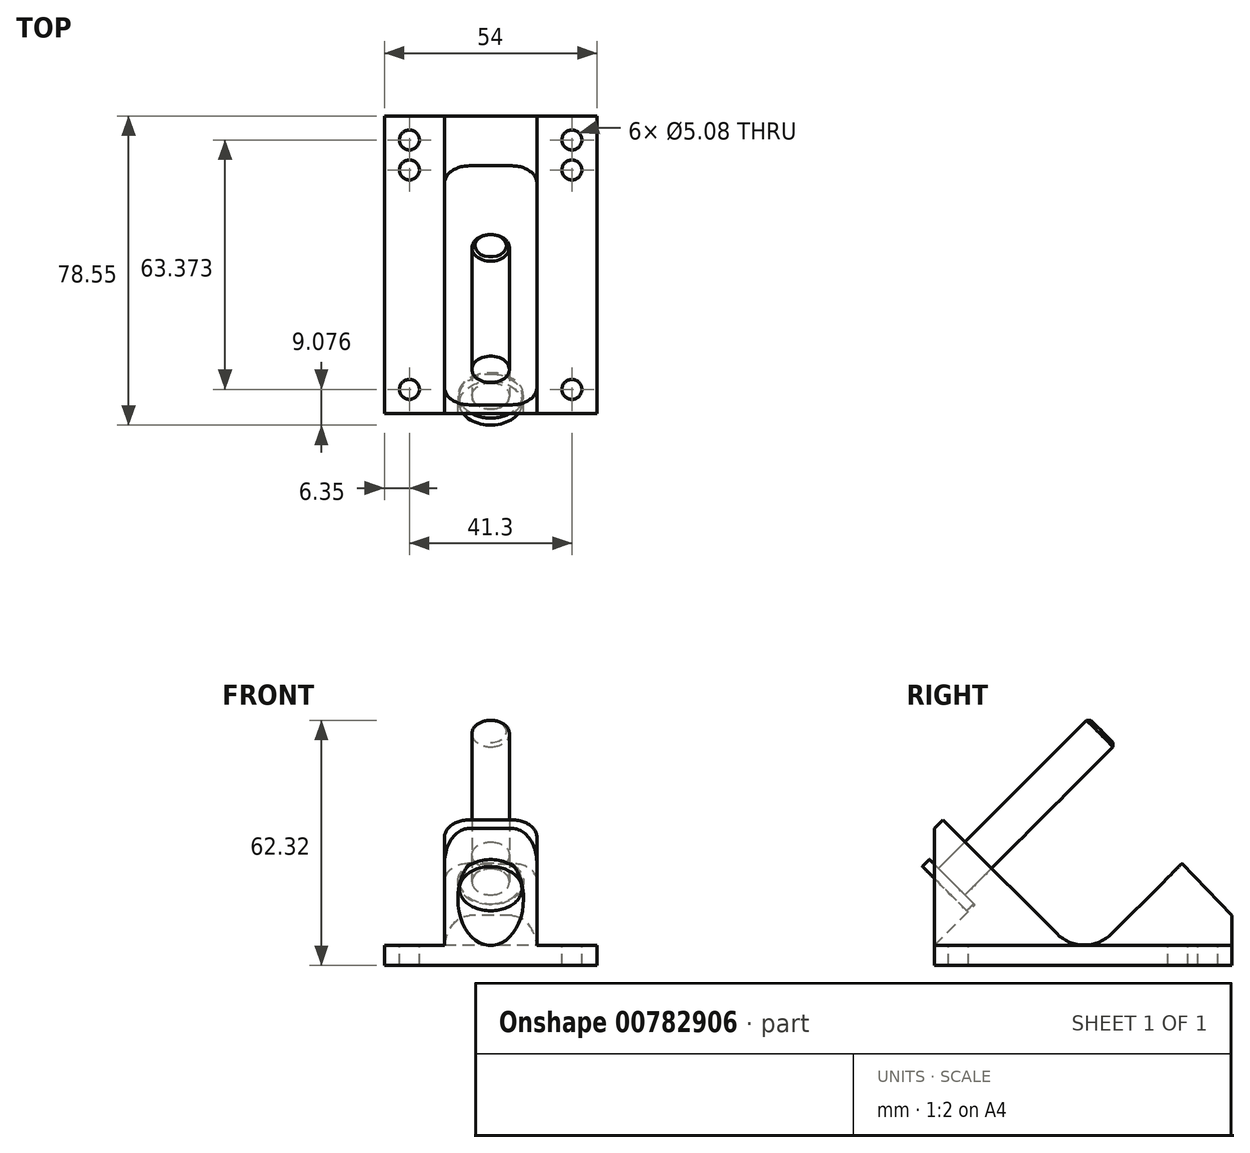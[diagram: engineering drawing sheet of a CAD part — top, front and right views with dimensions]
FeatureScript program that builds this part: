
annotation { "Feature Type Name" : "Feature", "Feature Type Description" : "" }
export const myFeature = defineFeature(function(context is Context, id is Id, definition is map)
    precondition{}
    {
        {
            var Q0;
            Q0=qCreatedBy(makeId("Right.planeOp"),FACE);
            var sketch = newSketch(context, id + "F0", { "sketchPlane" : qUnion([Q0])});
            skLineSegment(sketch, "E0", {"start": v(0, 0) * mm, "end": v(0, 34.86) * mm});
            skLineSegment(sketch, "E1", {"start": v(0, 34.86) * mm, "end": v(2.18, 37.04) * mm});
            skLineSegment(sketch, "E2", {"start": v(2.18, 37.04) * mm, "end": v(38.1, 1.12) * mm});
            skLineSegment(sketch, "E3", {"start": v(38.1, 1.12) * mm, "end": v(62.9, 25.92) * mm});
            skLineSegment(sketch, "E4", {"start": v(62.9, 25.92) * mm, "end": v(75.57, 12.7) * mm});
            skLineSegment(sketch, "E5", {"start": v(75.57, 12.7) * mm, "end": v(75.57, 0) * mm});
            skLineSegment(sketch, "E6", {"start": v(75.57, 0) * mm, "end": v(0, 0) * mm});
            skLineSegment(sketch, "E7", {"start": v(11.16, 28.06) * mm, "end": v(24.63, 41.53) * mm, "construction": true});
            skLineSegment(sketch, "E8", {"start": v(24.63, 41.53) * mm, "end": v(51.57, 14.59) * mm, "construction": true});
            skLineSegment(sketch, "E9", {"start": v(51.57, 14.59) * mm, "end": v(60.55, 5.6) * mm, "construction": true});
            skLineSegment(sketch, "E10", {"start": v(60.55, 5.6) * mm, "end": v(65.94, 11) * mm, "construction": true});
            skLineSegment(sketch, "E11", {"start": v(65.94, 11) * mm, "end": v(56.96, 19.98) * mm, "construction": true});
            skLineSegment(sketch, "E12", {"start": v(24.63, 41.53) * mm, "end": v(11.16, 55) * mm, "construction": true});
            skCircle(sketch, "E13", {"center": v(11.16, 55) * mm, "radius": 4 * mm, "construction": true});
            skLineSegment(sketch, "E14", {"start": v(60.55, 5.6) * mm, "end": v(55.16, 0.22) * mm, "construction": true});
            skLineSegment(sketch, "E15", {"start": v(55.16, 0.22) * mm, "end": v(46.18, 9.2) * mm, "construction": true});
            skCircle(sketch, "E16", {"center": v(54.26, 11.9) * mm, "radius": 5.08 * mm, "construction": true});
            skSolve(sketch);
        }
        {
            var Q0;
            Q0 = qSketchRegion(id + "F0", true);
            extrude(context, id + "F1", {"entities" : qUnion([Q0]), "depth" : 27 * mm, "offsetDistance" : 25.4 * mm});
        }
        {
            var Q0;
            Q0=makeQuery(id+"F1.opExtrude","SWEPT_EDGE",EDGE,{"disambiguationData":[OSD([sQuery(id+"F0.wireOp",EDGE,"E2"),sQuery(id+"F0.wireOp",EDGE,"E3")])]});
            fillet(context, id + "F2", {"entities" : qUnion([Q0]), "radius" : 9.9 * mm, "tangentPropagation" : true, "allowEdgeOverflow" : false});
        }
        {
            var Q0;
            Q0=makeQuery(id+"F1.opExtrude","CAP_FACE",FACE,{"disambiguationData":[OSD([sQuery(id+"F0.wireOp",EDGE,"E0"),sQuery(id+"F0.wireOp",EDGE,"E1"),sQuery(id+"F0.wireOp",EDGE,"E2"),sQuery(id+"F0.wireOp",EDGE,"E3"),sQuery(id+"F0.wireOp",EDGE,"E4"),sQuery(id+"F0.wireOp",EDGE,"E5"),sQuery(id+"F0.wireOp",EDGE,"E6")])],"isStart":false});
            var sketch = newSketch(context, id + "F3", { "sketchPlane" : qUnion([Q0])});
            skLineSegment(sketch, "E17.bottom", {"start": v(0, 5.08) * mm, "end": v(75.71, 5.08) * mm});
            skLineSegment(sketch, "E17.top", {"start": v(0, 37.04) * mm, "end": v(75.71, 37.04) * mm});
            skLineSegment(sketch, "E17.left", {"start": v(0, 5.08) * mm, "end": v(0, 37.04) * mm});
            skLineSegment(sketch, "E17.right", {"start": v(75.71, 5.08) * mm, "end": v(75.71, 37.04) * mm});
            skSolve(sketch);
        }
        {
            var Q0;
            Q0 = qSketchRegion(id + "F3", true);
            extrude(context, id + "F4", {"entities" : qUnion([Q0]), "operationType" : NewBodyOperationType.REMOVE, "oppositeDirection" : true, "depth" : 15.24 * mm, "offsetDistance" : 25.4 * mm});
        }
        {
            var Q0;
            Q0=makeQuery(id+"F4.boolean.opBoolean","COPY",FACE,{"derivedFrom":makeQuery(id+"F4.opExtrude","SWEPT_FACE",FACE,{"disambiguationData":[OSD([sQuery(id+"F3.wireOp",EDGE,"E17.bottom")])]})});
            var sketch = newSketch(context, id + "F5", { "sketchPlane" : qUnion([Q0])});
            skLineSegment(sketch, "E18", {"start": v(20.65, 69.47) * mm, "end": v(20.65, 61.85) * mm, "construction": true});
            skLineSegment(sketch, "E19", {"start": v(20.65, 61.85) * mm, "end": v(20.65, 6.1) * mm, "construction": true});
            skCircle(sketch, "E20", {"center": v(20.65, 69.47) * mm, "radius": 2.54 * mm});
            skCircle(sketch, "E21", {"center": v(20.65, 61.85) * mm, "radius": 2.54 * mm});
            skCircle(sketch, "E22", {"center": v(20.65, 6.1) * mm, "radius": 2.54 * mm});
            skSolve(sketch);
        }
        {
            var Q0;
            Q0 = qSketchRegion(id + "F5", true);
            extrude(context, id + "F6", {"entities" : qUnion([Q0]), "operationType" : NewBodyOperationType.REMOVE, "endBound" : BoundingType.THROUGH_ALL, "oppositeDirection" : true, "depth" : 25.4 * mm, "offsetDistance" : 25.4 * mm});
        }
        {
            var Q0;
            Q0=makeQuery(id+"F1.opExtrude","SWEPT_BODY",BODY,{"disambiguationData":[OSD([sQuery(id+"F0.wireOp",EDGE,"E0"),sQuery(id+"F0.wireOp",EDGE,"E1"),sQuery(id+"F0.wireOp",EDGE,"E2"),sQuery(id+"F0.wireOp",EDGE,"E3"),sQuery(id+"F0.wireOp",EDGE,"E4"),sQuery(id+"F0.wireOp",EDGE,"E5"),sQuery(id+"F0.wireOp",EDGE,"E6")])]});
            var Q1;
            Q1=makeQuery(id+"F0.imprint","IMPRINT",FACE,{"disambiguationData":[TD([[makeQuery(id+"F0.imprint","IMPRINT",EDGE,{"derivedFrom":sQuery(id+"F0.wireOp",EDGE,"E0")}),-1.0]])]});
            mirror(context, id + "F7", {"operationType" : NewBodyOperationType.ADD, "entities" : qUnion([Q0]), "mirrorPlane" : qUnion([Q1])});
        }
        {
            var Q0;
            Q0=makeQuery(id+"F7.opPattern","COPY",EDGE,{"derivedFrom":makeQuery(id+"F4.boolean.opBoolean","INTERSECT",EDGE,{"derivedFrom":[makeQuery(id+"F1.opExtrude","SWEPT_FACE",FACE,{"disambiguationData":[OSD([sQuery(id+"F0.wireOp",EDGE,"E4")])]}),makeQuery(id+"F4.opExtrude","CAP_FACE",FACE,{"disambiguationData":[OSD([sQuery(id+"F3.wireOp",EDGE,"E17.bottom"),sQuery(id+"F3.wireOp",EDGE,"E17.top"),sQuery(id+"F3.wireOp",EDGE,"E17.left"),sQuery(id+"F3.wireOp",EDGE,"E17.right")])],"isStart":false})]}),"instanceName":"1"});
            var Q1;
            Q1=makeQuery(id+"F4.boolean.opBoolean","INTERSECT",EDGE,{"derivedFrom":[makeQuery(id+"F1.opExtrude","SWEPT_FACE",FACE,{"disambiguationData":[OSD([sQuery(id+"F0.wireOp",EDGE,"E4")])]}),makeQuery(id+"F4.opExtrude","CAP_FACE",FACE,{"disambiguationData":[OSD([sQuery(id+"F3.wireOp",EDGE,"E17.bottom"),sQuery(id+"F3.wireOp",EDGE,"E17.top"),sQuery(id+"F3.wireOp",EDGE,"E17.left"),sQuery(id+"F3.wireOp",EDGE,"E17.right")])],"isStart":false})]});
            var Q2;
            Q2=makeQuery(id+"F7.opPattern","COPY",EDGE,{"derivedFrom":makeQuery(id+"F4.boolean.opBoolean","INTERSECT",EDGE,{"derivedFrom":[makeQuery(id+"F1.opExtrude","SWEPT_FACE",FACE,{"disambiguationData":[OSD([sQuery(id+"F0.wireOp",EDGE,"E1")])]}),makeQuery(id+"F4.opExtrude","CAP_FACE",FACE,{"disambiguationData":[OSD([sQuery(id+"F3.wireOp",EDGE,"E17.bottom"),sQuery(id+"F3.wireOp",EDGE,"E17.top"),sQuery(id+"F3.wireOp",EDGE,"E17.left"),sQuery(id+"F3.wireOp",EDGE,"E17.right")])],"isStart":false})]}),"instanceName":"1"});
            var Q3;
            Q3=makeQuery(id+"F4.boolean.opBoolean","INTERSECT",EDGE,{"derivedFrom":[makeQuery(id+"F1.opExtrude","SWEPT_FACE",FACE,{"disambiguationData":[OSD([sQuery(id+"F0.wireOp",EDGE,"E1")])]}),makeQuery(id+"F4.opExtrude","CAP_FACE",FACE,{"disambiguationData":[OSD([sQuery(id+"F3.wireOp",EDGE,"E17.bottom"),sQuery(id+"F3.wireOp",EDGE,"E17.top"),sQuery(id+"F3.wireOp",EDGE,"E17.left"),sQuery(id+"F3.wireOp",EDGE,"E17.right")])],"isStart":false})]});
            fillet(context, id + "F8", {"entities" : qUnion([Q0, Q1, Q2, Q3]), "radius" : 6.35 * mm, "tangentPropagation" : true, "allowEdgeOverflow" : false});
        }
        {
            var Q0;
            Q0=qCreatedBy(makeId("Right.planeOp"),FACE);
            var sketch = newSketch(context, id + "F9", { "sketchPlane" : qUnion([Q0])});
            skLineSegment(sketch, "E23.0", {"start": v(11.16, 28.06) * mm, "end": v(24.63, 41.53) * mm, "construction": true});
            skLineSegment(sketch, "E24", {"start": v(11.16, 28.06) * mm, "end": v(7.8, 31.43) * mm});
            skLineSegment(sketch, "E25", {"start": v(7.8, 31.43) * mm, "end": v(1.06, 24.7) * mm});
            skLineSegment(sketch, "E26", {"start": v(1.06, 24.7) * mm, "end": v(-1.48, 27.22) * mm});
            skLineSegment(sketch, "E27", {"start": v(-1.48, 27.22) * mm, "end": v(-14.35, 14.35) * mm});
            skLineSegment(sketch, "E28", {"start": v(-14.35, 14.35) * mm, "end": v(-8.45, 8.45) * mm});
            skLineSegment(sketch, "E29", {"start": v(-8.45, 8.45) * mm, "end": v(11.16, 28.06) * mm});
            skLineSegment(sketch, "E30", {"start": v(-8.45, 8.45) * mm, "end": v(0, 0) * mm, "construction": true});
            skLineSegment(sketch, "E31.0", {"start": v(2.18, 37.04) * mm, "end": v(38.1, 1.12) * mm});
            skSolve(sketch);
        }
        {
            var Q0;
            Q0 = qSketchRegion(id + "F9", true);
            var Q1;
            Q1=sQuery(id+"F9.wireOp",EDGE,"E23.0");
            revolve(context, id + "F10", {"operationType" : NewBodyOperationType.REMOVE, "surfaceOperationType" : NewSurfaceOperationType.NEW, "entities" : qUnion([Q0]), "axis" : qUnion([Q1]), "revolveType" : RevolveType.FULL, "oppositeDirection" : true});
        }
        {
            var Q0;
            Q0=qCreatedBy(makeId("Right.planeOp"),FACE);
            var sketch = newSketch(context, id + "F11", { "sketchPlane" : qUnion([Q0])});
            skLineSegment(sketch, "E32.1", {"start": v(1.06, 24.7) * mm, "end": v(-1.19, 26.94) * mm});
            skLineSegment(sketch, "E32.2", {"start": v(7.8, 31.43) * mm, "end": v(1.06, 24.7) * mm});
            skLineSegment(sketch, "E33", {"start": v(-1.19, 26.94) * mm, "end": v(-2.98, 25.14) * mm});
            skPoint(sketch, "E32.0.end.orphan", {"position": v(-14.35, 14.35) * mm});
            skPoint(sketch, "E32.0.start.orphan", {"position": v(-1.48, 27.22) * mm});
            skLineSegment(sketch, "E34", {"start": v(-2.98, 25.14) * mm, "end": v(2.63, 19.53) * mm});
            skLineSegment(sketch, "E35", {"start": v(2.63, 19.53) * mm, "end": v(42.6, 59.5) * mm});
            skLineSegment(sketch, "E36", {"start": v(42.6, 59.5) * mm, "end": v(39.22, 62.86) * mm});
            skLineSegment(sketch, "E37", {"start": v(39.22, 62.86) * mm, "end": v(7.8, 31.43) * mm});
            skSolve(sketch);
        }
        {
            var Q0;
            Q0 = qSketchRegion(id + "F11", true);
            var Q1;
            Q1=sQuery(id+"F11.wireOp",EDGE,"E35");
            revolve(context, id + "F12", {"surfaceOperationType" : NewSurfaceOperationType.NEW, "entities" : qUnion([Q0]), "axis" : qUnion([Q1]), "revolveType" : RevolveType.FULL});
        }
        {
            var Q0;
            Q0=makeQuery(id+"F12.opRevolve","SWEPT_FACE",FACE,{"disambiguationData":[OSD([sQuery(id+"F11.wireOp",EDGE,"E36")])]});
            chamfer(context, id + "F13", {"entities" : qUnion([Q0]), "width" : 0.76 * mm, "tangentPropagation" : true});
        }
    });
